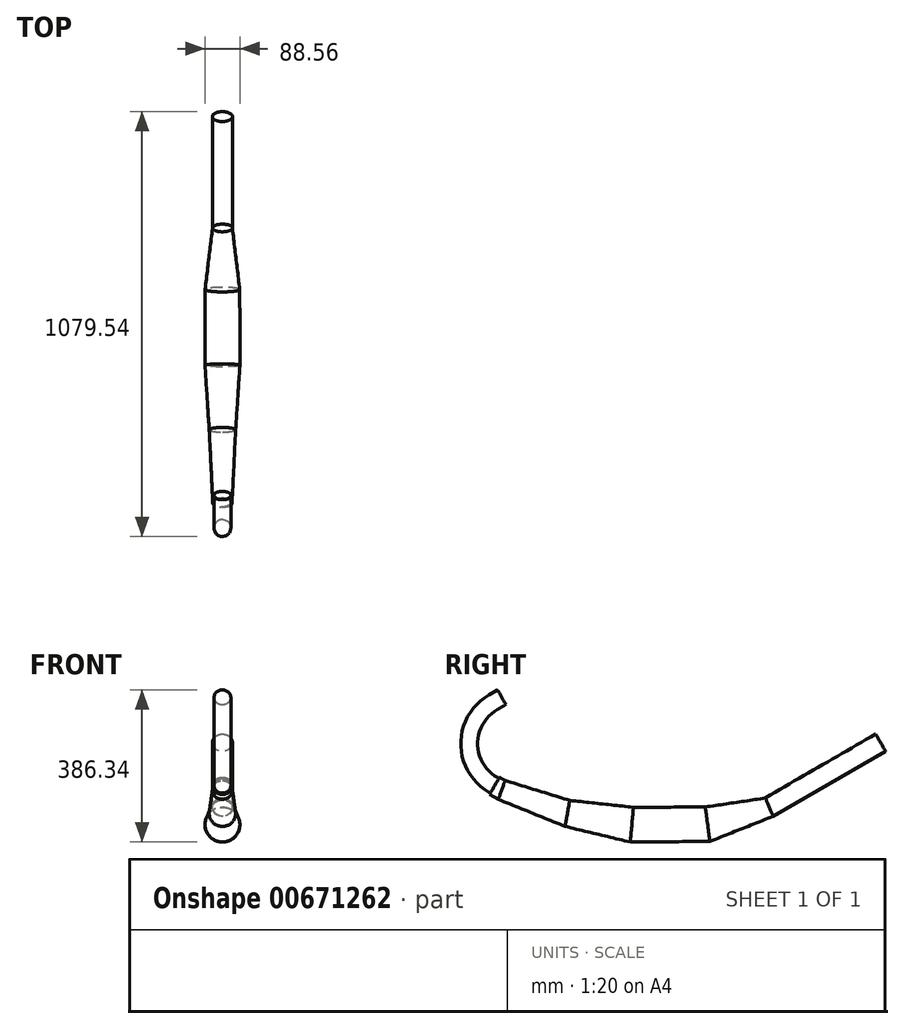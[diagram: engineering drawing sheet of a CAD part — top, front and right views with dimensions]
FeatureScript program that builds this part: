
annotation { "Feature Type Name" : "Feature", "Feature Type Description" : "" }
export const myFeature = defineFeature(function(context is Context, id is Id, definition is map)
    precondition{}
    {
        {
            var Q0;
            Q0=qCreatedBy(makeId("Front.planeOp"),FACE);
            var sketch = newSketch(context, id + "F0", { "sketchPlane" : qUnion([Q0])});
            skCircle(sketch, "E0", {"center": v(0, 0) * mm, "radius": 21.43 * mm});
            skLineSegment(sketch, "E1", {"start": v(0, 0) * mm, "end": v(0, -121.29) * mm});
            skLineSegment(sketch, "E2", {"start": v(0, -121.29) * mm, "end": v(-25.4, -121.29) * mm});
            skLineSegment(sketch, "E3", {"start": v(-25.4, -121.29) * mm, "end": v(25.4, -121.29) * mm});
            skSolve(sketch);
        }
        {
            var Q0;
            Q0=makeQuery(id+"F0.imprint","IMPRINT",FACE,{"disambiguationData":[TD([[makeQuery(id+"F0.imprint","IMPRINT",EDGE,{"derivedFrom":sQuery(id+"F0.wireOp",EDGE,"E0")}),1.0]])]});
            var Q1;
            Q1=sQuery(id+"F0.wireOp",EDGE,"E0");
            var Q2;
            Q2=sQuery(id+"F0.wireOp",EDGE,"E3");
            revolve(context, id + "F1", {"entities" : qUnion([Q0]), "surfaceEntities" : qUnion([Q1]), "axis" : qUnion([Q2]), "revolveType" : RevolveType.TWO_DIRECTIONS, "angle" : 150 * degree, "angleBack" : 30 * degree});
        }
        {
            var Q0;
            Q0=makeQuery(id+"F1.opRevolve","CAP_FACE",FACE,{"disambiguationData":[OSD([sQuery(id+"F0.wireOp",EDGE,"E0")])],"isStart":true});
            extrude(context, id + "F2", {"entities" : qUnion([Q0]), "operationType" : NewBodyOperationType.ADD, "depth" : 25.4 * mm, "offsetDistance" : 25.4 * mm});
        }
        {
            var Q0;
            Q0=makeQuery(id+"F1.opRevolve","CAP_FACE",FACE,{"disambiguationData":[OSD([sQuery(id+"F0.wireOp",EDGE,"E0")])],"isStart":false});
            extrude(context, id + "F3", {"entities" : qUnion([Q0]), "operationType" : NewBodyOperationType.ADD, "depth" : 25.4 * mm, "offsetDistance" : 25.4 * mm});
        }
        {
            var Q0;
            Q0=qCreatedBy(makeId("Right.planeOp"),FACE);
            var sketch = newSketch(context, id + "F4", { "sketchPlane" : qUnion([Q0])});
            skLineSegment(sketch, "E4.0.0", {"start": v(-27.93, -220.46) * mm, "end": v(-49.36, -257.58) * mm});
            skLineSegment(sketch, "E5", {"start": v(-38.65, -239.02) * mm, "end": v(122.46, -297.66) * mm});
            skLineSegment(sketch, "E6", {"start": v(134.14, -265.59) * mm, "end": v(110.8, -329.73) * mm});
            skLineSegment(sketch, "E7", {"start": v(122.46, -297.66) * mm, "end": v(288.18, -326.88) * mm});
            skLineSegment(sketch, "E8", {"start": v(288.18, -326.88) * mm, "end": v(478.68, -326.88) * mm});
            skLineSegment(sketch, "E9", {"start": v(478.68, -371.33) * mm, "end": v(478.68, -282.43) * mm});
            skLineSegment(sketch, "E10", {"start": v(478.68, -326.88) * mm, "end": v(638.16, -284.15) * mm});
            skLineSegment(sketch, "E11", {"start": v(644.73, -308.68) * mm, "end": v(631.58, -259.62) * mm});
            skLineSegment(sketch, "E12", {"start": v(638.16, -284.15) * mm, "end": v(924.12, -119.05) * mm});
            skLineSegment(sketch, "E13", {"start": v(-38.65, -239.02) * mm, "end": v(-82.64, -213.62) * mm});
            skLineSegment(sketch, "E14", {"start": v(936.82, -141.05) * mm, "end": v(911.42, -97.05) * mm});
            skLineSegment(sketch, "E15", {"start": v(631.58, -259.62) * mm, "end": v(478.68, -282.43) * mm});
            skLineSegment(sketch, "E16", {"start": v(631.58, -259.62) * mm, "end": v(911.42, -97.05) * mm});
            skLineSegment(sketch, "E17", {"start": v(650.86, -306.15) * mm, "end": v(625.46, -262.15) * mm});
            skLineSegment(sketch, "E18", {"start": v(650.86, -306.15) * mm, "end": v(936.82, -141.05) * mm});
            skLineSegment(sketch, "E19", {"start": v(490.19, -369.82) * mm, "end": v(467.18, -283.95) * mm});
            skLineSegment(sketch, "E20", {"start": v(650.86, -306.15) * mm, "end": v(490.19, -369.82) * mm});
            skLineSegment(sketch, "E21", {"start": v(122.46, -331.8) * mm, "end": v(122.46, -263.53) * mm});
            skLineSegment(sketch, "E22", {"start": v(-47.33, -262.89) * mm, "end": v(-29.96, -215.15) * mm});
            skLineSegment(sketch, "E23", {"start": v(134.14, -265.59) * mm, "end": v(-29.96, -215.15) * mm});
            skLineSegment(sketch, "E24", {"start": v(-47.33, -262.89) * mm, "end": v(122.46, -331.8) * mm});
            skLineSegment(sketch, "E25", {"start": v(134.14, -265.59) * mm, "end": v(122.46, -331.8) * mm});
            skLineSegment(sketch, "E26", {"start": v(478.68, -282.43) * mm, "end": v(490.19, -369.82) * mm});
            skLineSegment(sketch, "E27", {"start": v(631.58, -259.62) * mm, "end": v(650.86, -306.15) * mm});
            skLineSegment(sketch, "E28", {"start": v(288.18, -371.33) * mm, "end": v(288.18, -282.43) * mm});
            skLineSegment(sketch, "E29", {"start": v(280.46, -370.66) * mm, "end": v(295.9, -283.1) * mm});
            skLineSegment(sketch, "E30", {"start": v(134.14, -265.59) * mm, "end": v(295.9, -283.1) * mm});
            skLineSegment(sketch, "E31", {"start": v(295.9, -283.1) * mm, "end": v(478.68, -282.43) * mm});
            skLineSegment(sketch, "E32", {"start": v(122.46, -331.8) * mm, "end": v(288.18, -371.33) * mm});
            skLineSegment(sketch, "E33", {"start": v(490.19, -369.82) * mm, "end": v(288.18, -371.33) * mm});
            skLineSegment(sketch, "E34", {"start": v(295.9, -283.1) * mm, "end": v(288.18, -371.33) * mm});
            skLineSegment(sketch, "E35", {"start": v(-44.32, -206.86) * mm, "end": v(-69.33, -250.19) * mm});
            skLineSegment(sketch, "E36", {"start": v(-47.33, -262.89) * mm, "end": v(-22.32, -219.56) * mm});
            skLineSegment(sketch, "E37", {"start": v(-44.32, -206.86) * mm, "end": v(-22.32, -219.56) * mm});
            skLineSegment(sketch, "E38", {"start": v(-47.33, -262.89) * mm, "end": v(-69.33, -250.19) * mm});
            skLineSegment(sketch, "E39", {"start": v(631.58, -259.62) * mm, "end": v(873.93, -223.45) * mm, "construction": true});
            skLineSegment(sketch, "E40", {"start": v(650.86, -306.15) * mm, "end": v(872.57, -218.29) * mm, "construction": true});
            skLineSegment(sketch, "E41", {"start": v(484.44, -326.12) * mm, "end": v(850.84, -226.9) * mm, "construction": true});
            skLineSegment(sketch, "E42", {"start": v(484.44, -326.12) * mm, "end": v(292.04, -327.22) * mm, "construction": true});
            skLineSegment(sketch, "E43", {"start": v(292.04, -327.22) * mm, "end": v(128.3, -298.69) * mm, "construction": true});
            skLineSegment(sketch, "E44", {"start": v(128.3, -298.69) * mm, "end": v(-38.65, -239.02) * mm, "construction": true});
            skSolve(sketch);
        }
        {
            var Q0;
            Q0=sQuery(id+"F4.wireOp",EDGE,"E36");
            cPlane(context, id + "F5", {"entities" : qUnion([Q0]), "cplaneType" : CPlaneType.LINE_ANGLE, "offset" : 25.4 * mm, "angle" : 90 * degree, "width" : 152.4 * mm, "height" : 152.4 * mm});
        }
        {
            var Q0;
            Q0=qCreatedBy(id+"F5.planeOp",FACE);
            var sketch = newSketch(context, id + "F6", { "sketchPlane" : qUnion([Q0])});
            skLineSegment(sketch, "E45.0", {"start": v(0, -251.34) * mm, "end": v(0, -201.3) * mm, "construction": true});
            skCircle(sketch, "E46", {"center": v(0, -226.32) * mm, "radius": 25.01 * mm});
            skSolve(sketch);
        }
        {
            var Q0;
            Q0=makeQuery(id+"F6.imprint","IMPRINT",FACE,{"disambiguationData":[TD([[makeQuery(id+"F6.imprint","IMPRINT",EDGE,{"derivedFrom":sQuery(id+"F6.wireOp",EDGE,"E46")}),1.0]])]});
            var Q1;
            Q1=sQuery(id+"F6.wireOp",EDGE,"E46");
            extrude(context, id + "F7", {"entities" : qUnion([Q0]), "surfaceEntities" : qUnion([Q1]), "oppositeDirection" : true, "depth" : 25.4 * mm, "offsetDistance" : 25.4 * mm});
        }
        {
            var Q0;
            Q0=sQuery(id+"F4.wireOp",EDGE,"E22");
            cPlane(context, id + "F8", {"entities" : qUnion([Q0]), "cplaneType" : CPlaneType.LINE_ANGLE, "offset" : 25.4 * mm, "angle" : 90 * degree, "width" : 152.4 * mm, "height" : 152.4 * mm});
        }
        {
            var Q0;
            Q0=qCreatedBy(id+"F8.planeOp",FACE);
            var sketch = newSketch(context, id + "F9", { "sketchPlane" : qUnion([Q0])});
            skLineSegment(sketch, "E47.0", {"start": v(0, -263.22) * mm, "end": v(0, -212.42) * mm, "construction": true});
            skCircle(sketch, "E48", {"center": v(0, -237.82) * mm, "radius": 25.4 * mm});
            skSolve(sketch);
        }
        {
            var Q0;
            Q0=sQuery(id+"F4.wireOp",EDGE,"E25");
            cPlane(context, id + "F10", {"entities" : qUnion([Q0]), "cplaneType" : CPlaneType.LINE_ANGLE, "offset" : 25.4 * mm, "angle" : 90 * degree, "oppositeDirection" : true, "width" : 152.4 * mm, "height" : 152.4 * mm});
        }
        {
            var Q0;
            Q0=qCreatedBy(id+"F10.planeOp",FACE);
            var sketch = newSketch(context, id + "F11", { "sketchPlane" : qUnion([Q0])});
            skLineSegment(sketch, "E49.0", {"start": v(0, -238.26) * mm, "end": v(0, -305.49) * mm, "construction": true});
            skCircle(sketch, "E50", {"center": v(0, -271.87) * mm, "radius": 33.61 * mm});
            skSolve(sketch);
        }
        {
            var Q1;
            Q1=makeQuery(id+"F9.imprint","IMPRINT",FACE,{"disambiguationData":[TD([[makeQuery(id+"F9.imprint","IMPRINT",EDGE,{"derivedFrom":sQuery(id+"F9.wireOp",EDGE,"E48")}),1.0]])]});
            var Q2;
            Q2=makeQuery(id+"F11.imprint","IMPRINT",FACE,{"disambiguationData":[TD([[makeQuery(id+"F11.imprint","IMPRINT",EDGE,{"derivedFrom":sQuery(id+"F11.wireOp",EDGE,"E50")}),1.0]])]});
            var Q3;
            Q3=sQuery(id+"F4.wireOp",EDGE,"E23");
            var Q4;
            Q4=sQuery(id+"F4.wireOp",EDGE,"E24");
            loft(context, id + "F12", {"operationType" : NewBodyOperationType.ADD, "addGuides" : true, "sheetProfilesArray" : [{ "sheetProfileEntities" : qUnion([Q1]) }, { "sheetProfileEntities" : qUnion([Q2]) }], "guidesArray" : [{ "guideEntities" : qUnion([Q3]), "guideDerivativeType" : LoftGuideDerivativeType.DEFAULT, "guideDerivativeMagnitude" : 1 }, { "guideEntities" : qUnion([Q4]), "guideDerivativeType" : LoftGuideDerivativeType.DEFAULT, "guideDerivativeMagnitude" : 1 }]});
        }
        {
            var Q0;
            Q0=sQuery(id+"F4.wireOp",EDGE,"E34");
            cPlane(context, id + "F13", {"entities" : qUnion([Q0]), "cplaneType" : CPlaneType.LINE_ANGLE, "offset" : 25.4 * mm, "angle" : 90 * degree, "width" : 152.4 * mm, "height" : 152.4 * mm});
        }
        {
            var Q0;
            Q0=qCreatedBy(id+"F13.planeOp",FACE);
            var sketch = newSketch(context, id + "F14", { "sketchPlane" : qUnion([Q0])});
            skLineSegment(sketch, "E51.0", {"start": v(0, -256.24) * mm, "end": v(0, -344.8) * mm, "construction": true});
            skCircle(sketch, "E52", {"center": v(0, -300.52) * mm, "radius": 44.28 * mm});
            skSolve(sketch);
        }
        {
            var Q1;
            Q1=makeQuery(id+"F12.opLoft","CAP_FACE",FACE,{"disambiguationData":[OSD([makeQuery(id+"F11.imprint","IMPRINT",FACE,{"disambiguationData":[TD([[makeQuery(id+"F11.imprint","IMPRINT",EDGE,{"derivedFrom":sQuery(id+"F11.wireOp",EDGE,"E50")}),1.0]])]})])],"isStart":true});
            var Q2;
            Q2=makeQuery(id+"F14.imprint","IMPRINT",FACE,{"disambiguationData":[TD([[makeQuery(id+"F14.imprint","IMPRINT",EDGE,{"derivedFrom":sQuery(id+"F14.wireOp",EDGE,"E52")}),1.0]])]});
            var Q3;
            Q3=sQuery(id+"F4.wireOp",EDGE,"E30");
            var Q4;
            Q4=sQuery(id+"F4.wireOp",EDGE,"E32");
            loft(context, id + "F15", {"addGuides" : true, "sheetProfilesArray" : [{ "sheetProfileEntities" : qUnion([Q1]) }, { "sheetProfileEntities" : qUnion([Q2]) }], "guidesArray" : [{ "guideEntities" : qUnion([Q3]), "guideDerivativeType" : LoftGuideDerivativeType.DEFAULT, "guideDerivativeMagnitude" : 1 }, { "guideEntities" : qUnion([Q4]), "guideDerivativeType" : LoftGuideDerivativeType.DEFAULT, "guideDerivativeMagnitude" : 1 }]});
        }
        {
            var Q0;
            Q0=sQuery(id+"F4.wireOp",EDGE,"E26");
            cPlane(context, id + "F16", {"entities" : qUnion([Q0]), "cplaneType" : CPlaneType.LINE_ANGLE, "offset" : 25.4 * mm, "angle" : 90 * degree, "width" : 152.4 * mm, "height" : 152.4 * mm});
        }
        {
            var Q0;
            Q0=qCreatedBy(id+"F16.planeOp",FACE);
            var sketch = newSketch(context, id + "F17", { "sketchPlane" : qUnion([Q0])});
            skLineSegment(sketch, "E53.0", {"start": v(0, -342.5) * mm, "end": v(0, -430.63) * mm, "construction": true});
            skCircle(sketch, "E54", {"center": v(0, -386.57) * mm, "radius": 44.07 * mm});
            skSolve(sketch);
        }
        {
            var Q1;
            Q1=makeQuery(id+"F15.opLoft","CAP_FACE",FACE,{"disambiguationData":[OSD([makeQuery(id+"F14.imprint","IMPRINT",FACE,{"disambiguationData":[TD([[makeQuery(id+"F14.imprint","IMPRINT",EDGE,{"derivedFrom":sQuery(id+"F14.wireOp",EDGE,"E52")}),1.0]])]})])],"isStart":true});
            var Q2;
            Q2=makeQuery(id+"F17.imprint","IMPRINT",FACE,{"disambiguationData":[TD([[makeQuery(id+"F17.imprint","IMPRINT",EDGE,{"derivedFrom":sQuery(id+"F17.wireOp",EDGE,"E54")}),1.0]])]});
            var Q3;
            Q3=makeQuery(id+"F15.opLoft","CAP_FACE",FACE,{"disambiguationData":[OSD([makeQuery(id+"F14.imprint","IMPRINT",FACE,{"disambiguationData":[TD([[makeQuery(id+"F14.imprint","IMPRINT",EDGE,{"derivedFrom":sQuery(id+"F14.wireOp",EDGE,"E52")}),1.0]])]})])],"isStart":true});
            var Q4;
            Q4=makeQuery(id+"F17.imprint","IMPRINT",FACE,{"disambiguationData":[TD([[makeQuery(id+"F17.imprint","IMPRINT",EDGE,{"derivedFrom":sQuery(id+"F17.wireOp",EDGE,"E54")}),1.0]])]});
            var Q5;
            Q5=sQuery(id+"F4.wireOp",EDGE,"E31");
            var Q6;
            Q6=sQuery(id+"F4.wireOp",EDGE,"E33");
            loft(context, id + "F18", {"addGuides" : true, "sheetProfilesArray" : [{ "sheetProfileEntities" : qUnion([Q1]) }, { "sheetProfileEntities" : qUnion([Q2]) }], "wireProfilesArray" : [{ "wireProfileEntities" : qUnion([Q3]) }, { "wireProfileEntities" : qUnion([Q4]) }], "guidesArray" : [{ "guideEntities" : qUnion([Q5]), "guideDerivativeType" : LoftGuideDerivativeType.DEFAULT, "guideDerivativeMagnitude" : 1 }, { "guideEntities" : qUnion([Q6]), "guideDerivativeType" : LoftGuideDerivativeType.DEFAULT, "guideDerivativeMagnitude" : 1 }]});
        }
        {
            var Q0;
            Q0=sQuery(id+"F4.wireOp",EDGE,"E27");
            cPlane(context, id + "F19", {"entities" : qUnion([Q0]), "cplaneType" : CPlaneType.LINE_ANGLE, "offset" : 25.4 * mm, "angle" : 90 * degree, "width" : 152.4 * mm, "height" : 152.4 * mm});
        }
        {
            var Q0;
            Q0=qCreatedBy(id+"F19.planeOp",FACE);
            var sketch = newSketch(context, id + "F20", { "sketchPlane" : qUnion([Q0])});
            skLineSegment(sketch, "E55.0", {"start": v(0, -481.55) * mm, "end": v(0, -531.92) * mm, "construction": true});
            skCircle(sketch, "E56", {"center": v(0, -506.73) * mm, "radius": 25.18 * mm});
            skSolve(sketch);
        }
        {
            var Q1;
            Q1=makeQuery(id+"F18.opLoft","CAP_FACE",FACE,{"disambiguationData":[OSD([makeQuery(id+"F17.imprint","IMPRINT",FACE,{"disambiguationData":[TD([[makeQuery(id+"F17.imprint","IMPRINT",EDGE,{"derivedFrom":sQuery(id+"F17.wireOp",EDGE,"E54")}),1.0]])]})])],"isStart":true});
            var Q2;
            Q2=makeQuery(id+"F20.imprint","IMPRINT",FACE,{"disambiguationData":[TD([[makeQuery(id+"F20.imprint","IMPRINT",EDGE,{"derivedFrom":sQuery(id+"F20.wireOp",EDGE,"E56")}),1.0]])]});
            var Q3;
            Q3=sQuery(id+"F4.wireOp",EDGE,"E15");
            var Q4;
            Q4=sQuery(id+"F4.wireOp",EDGE,"E20");
            loft(context, id + "F21", {"addGuides" : true, "sheetProfilesArray" : [{ "sheetProfileEntities" : qUnion([Q1]) }, { "sheetProfileEntities" : qUnion([Q2]) }], "guidesArray" : [{ "guideEntities" : qUnion([Q3]), "guideDerivativeType" : LoftGuideDerivativeType.DEFAULT, "guideDerivativeMagnitude" : 1 }, { "guideEntities" : qUnion([Q4]), "guideDerivativeType" : LoftGuideDerivativeType.DEFAULT, "guideDerivativeMagnitude" : 1 }]});
        }
        {
            var Q0;
            Q0=sQuery(id+"F4.wireOp",EDGE,"E14");
            cPlane(context, id + "F22", {"entities" : qUnion([Q0]), "cplaneType" : CPlaneType.LINE_ANGLE, "offset" : 25.4 * mm, "angle" : 90 * degree, "width" : 152.4 * mm, "height" : 152.4 * mm});
        }
        {
            var Q0;
            Q0=qCreatedBy(id+"F22.planeOp",FACE);
            var sketch = newSketch(context, id + "F23", { "sketchPlane" : qUnion([Q0])});
            skLineSegment(sketch, "E57.0", {"start": v(0, -590.56) * mm, "end": v(0, -539.76) * mm, "construction": true});
            skCircle(sketch, "E58", {"center": v(0, -565.16) * mm, "radius": 25.4 * mm});
            skSolve(sketch);
        }
        {
            var Q0;
            Q0=makeQuery(id+"F23.imprint","IMPRINT",FACE,{"disambiguationData":[TD([[makeQuery(id+"F23.imprint","IMPRINT",EDGE,{"derivedFrom":sQuery(id+"F23.wireOp",EDGE,"E58")}),1.0]])]});
            var Q1;
            Q1=sQuery(id+"F23.wireOp",EDGE,"E58");
            var Q2;
            Q2=makeQuery(id+"F21.opLoft","CAP_FACE",FACE,{"disambiguationData":[OSD([makeQuery(id+"F20.imprint","IMPRINT",FACE,{"disambiguationData":[TD([[makeQuery(id+"F20.imprint","IMPRINT",EDGE,{"derivedFrom":sQuery(id+"F20.wireOp",EDGE,"E56")}),1.0]])]})])],"isStart":true});
            extrude(context, id + "F24", {"entities" : qUnion([Q0]), "surfaceEntities" : qUnion([Q1]), "endBound" : BoundingType.UP_TO_SURFACE, "oppositeDirection" : true, "depth" : 25.4 * mm, "endBoundEntityFace" : qUnion([Q2]), "offsetDistance" : 25.4 * mm});
        }
    });
